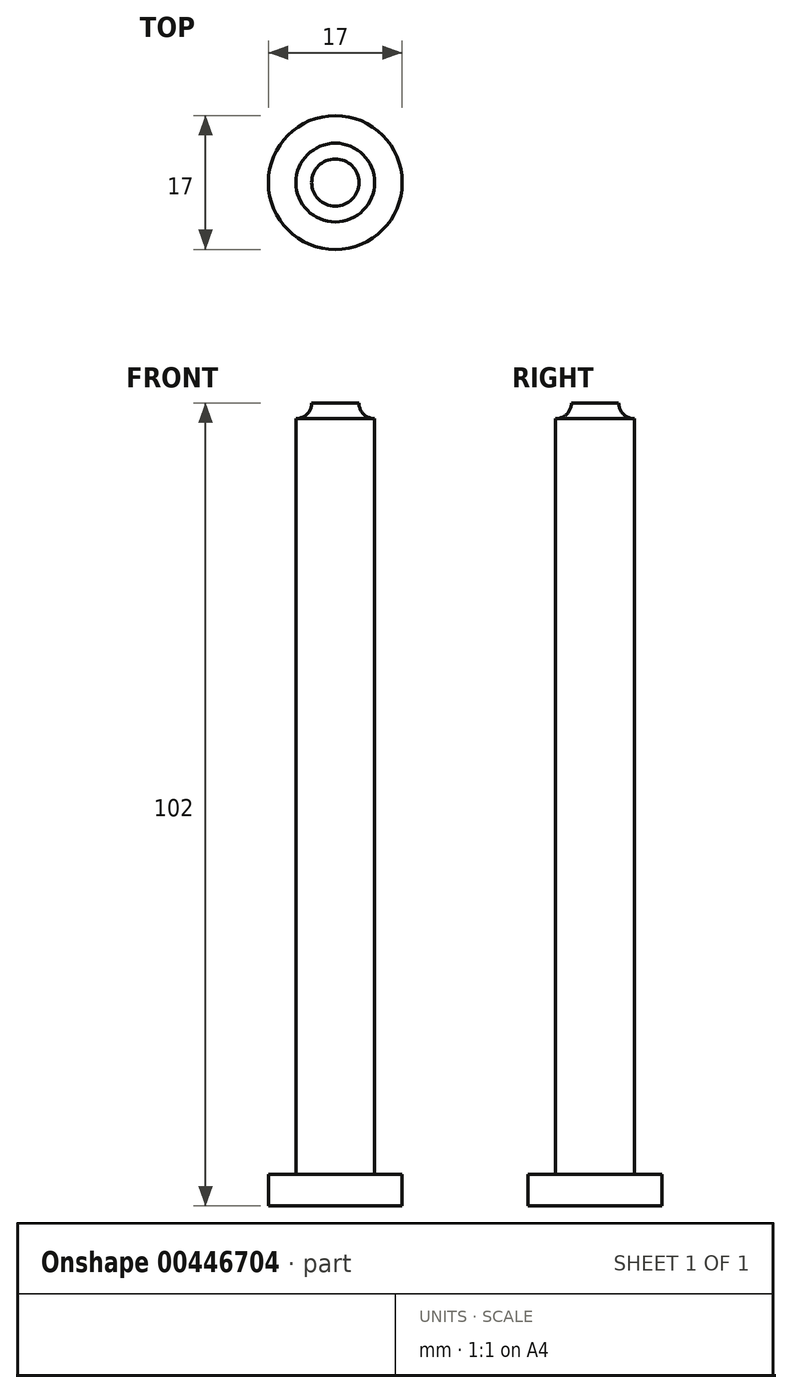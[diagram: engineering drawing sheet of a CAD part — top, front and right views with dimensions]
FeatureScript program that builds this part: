
annotation { "Feature Type Name" : "Feature", "Feature Type Description" : "" }
export const myFeature = defineFeature(function(context is Context, id is Id, definition is map)
    precondition{}
    {
        {
            var Q0;
            Q0=qCreatedBy(makeId("Top.planeOp"),FACE);
            var sketch = newSketch(context, id + "F0", { "sketchPlane" : qUnion([Q0])});
            skCircle(sketch, "E0", {"center": v(0, 0) * mm, "radius": 8.5 * mm});
            skSolve(sketch);
        }
        {
            var Q0;
            Q0=qSketchRegion(id+"F0",true);
            extrude(context, id + "F1", {"entities" : qUnion([Q0]), "depth" : 4 * mm});
        }
        {
            var Q0;
            Q0=qCreatedBy(makeId("Top.planeOp"),FACE);
            var sketch = newSketch(context, id + "F2", { "sketchPlane" : qUnion([Q0])});
            skCircle(sketch, "E1", {"center": v(0, 0) * mm, "radius": 5 * mm});
            skSolve(sketch);
        }
        {
            var Q0;
            Q0=qSketchRegion(id+"F2",true);
            extrude(context, id + "F3", {"entities" : qUnion([Q0]), "operationType" : NewBodyOperationType.ADD, "depth" : 100 * mm});
        }
        {
            var Q0;
            Q0=qCreatedBy(makeId("Right.planeOp"),FACE);
            var sketch = newSketch(context, id + "F4", { "sketchPlane" : qUnion([Q0])});
            skLineSegment(sketch, "E2", {"start": v(0, 100) * mm, "end": v(0, 102) * mm});
            skLineSegment(sketch, "E3", {"start": v(0, 102) * mm, "end": v(3, 102) * mm});
            skLineSegment(sketch, "E4", {"start": v(5, 100) * mm, "end": v(0, 100) * mm});
            skArc(sketch, "E5", {"start": v(3, 102) * mm, "mid": v(3.59, 100.59) * mm, "end": v(5, 100) * mm});
            skSolve(sketch);
        }
        {
            var Q0;
            Q0=qSketchRegion(id+"F4",true);
            var Q1;
            Q1=sQuery(id+"F4.wireOp",EDGE,"E2");
            revolve(context, id + "F5", {"operationType" : NewBodyOperationType.ADD, "entities" : qUnion([Q0]), "axis" : qUnion([Q1]), "revolveType" : RevolveType.FULL});
        }
    });
